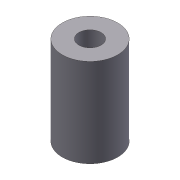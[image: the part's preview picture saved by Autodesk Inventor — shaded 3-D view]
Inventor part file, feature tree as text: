
AUTODESK INVENTOR PART (.ipt)
format: ipt  version: 2012 (Build 160160000, 160)  size: 71,168 bytes
history: native  units: in
note: dims shown in document units (in); Inventor stores cm internally (conversion verified against a paired STEP export)
features: extrude x1, sketch x1
ambient origin geometry x8: Origin, YZ Plane, XZ Plane, XY Plane, X Axis, Y Axis, Z Axis, Center Point
bodies: Solid1 (feature_tree)
feature tree (2):
  extrude  "Extrusion1"  Depth=0.25in
  sketch  "Sketch2"  dims[d0=0.625in d1=0.25in d2=1.0in d3=0.0in]
